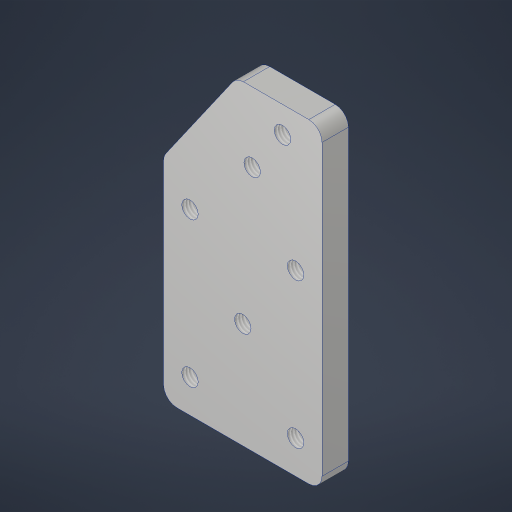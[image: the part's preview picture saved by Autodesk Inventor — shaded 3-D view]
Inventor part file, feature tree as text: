
AUTODESK INVENTOR PART (.ipt)
format: ipt  version: 2023.4 (Build 274418000, 418)  size: 234,496 bytes
history: native  units: in
note: dims shown in document units (in); Inventor stores cm internally (conversion verified against a paired STEP export)
features: sketch x1, extrude x1, hole x1, fillet x1
ambient origin geometry x8: Origin, YZ Plane, XZ Plane, XY Plane, X Axis, Y Axis, Z Axis, Center Point
bodies: Solid1 (feature_tree)
feature tree (4):
  sketch  "Sketch1"  dims[d0=2.0in d1=14.0in d2=0.3779in d3=1.0in d4=2.0in d5=15.25in d6=17.0in d10=0.5in d11=0.3125in d12=1.0in d13=0.3125in d14=5.9055in d16=1.0in d17=0.3937in d19=1.0in d21=1.375in d22=1.25in d23=1.25in d24=1.25in d25=4.75in d26=1.25in d27=3.0in d28=0.75in d29=1.5748in d31=0.5in d32=0.3937in d34=1.0in d37=0.25in d38=0.25in d39=0.25in d40=0.201in d41=0.25in d42=0.0in d43=0.156in d44=0.38in d45=0.375in d46=0.25in d47=0.5635in d48=1.0in d49=0.8108in d50=0.125in]
  extrude  "Extrusion1"  Depth=0.125in
  hole  "Hole1"  [1 undecoded]
  fillet  "Fillet1"  Radius=1.0in
note: 1 required parameter value undecoded (feature->parameter linkage not recoverable at this tier; creation-order binding heuristic only, values carry confidence <= 0.55)
